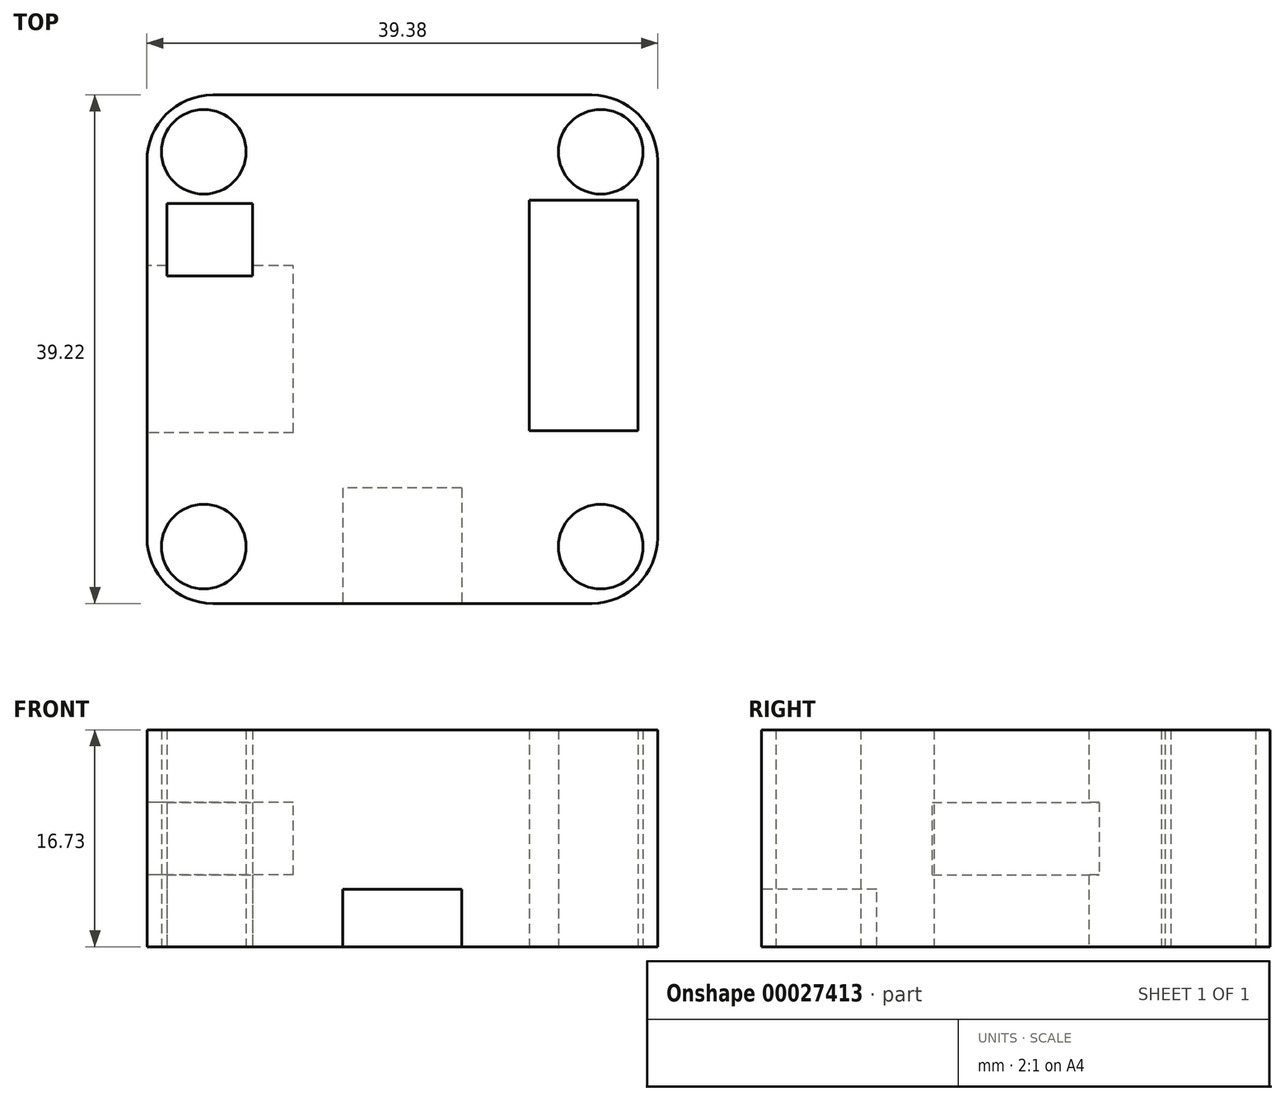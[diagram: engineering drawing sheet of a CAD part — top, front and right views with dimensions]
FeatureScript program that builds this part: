
annotation { "Feature Type Name" : "Feature", "Feature Type Description" : "" }
export const myFeature = defineFeature(function(context is Context, id is Id, definition is map)
    precondition{}
    {
        {
            var Q0;
            Q0=qCreatedBy(makeId("Top.planeOp"),FACE);
            var sketch = newSketch(context, id + "F0", { "sketchPlane" : qUnion([Q0])});
            skLineSegment(sketch, "E0.rect.bottom", {"start": v(19.69, -19.6) * mm, "end": v(-19.69, -19.6) * mm});
            skLineSegment(sketch, "E0.rect.top", {"start": v(19.69, 19.6) * mm, "end": v(-19.69, 19.6) * mm});
            skLineSegment(sketch, "E0.rect.left", {"start": v(19.69, -19.6) * mm, "end": v(19.69, 19.6) * mm});
            skLineSegment(sketch, "E0.rect.right", {"start": v(-19.69, -19.6) * mm, "end": v(-19.69, 19.6) * mm});
            skPoint(sketch, "E0.rect.middle", {"position": v(0, 0) * mm});
            skLineSegment(sketch, "E1.bottom", {"start": v(9.78, 11.5) * mm, "end": v(18.19, 11.5) * mm});
            skLineSegment(sketch, "E1.top", {"start": v(9.78, -6.3) * mm, "end": v(18.19, -6.3) * mm});
            skLineSegment(sketch, "E1.left", {"start": v(9.78, 11.5) * mm, "end": v(9.78, -6.3) * mm});
            skLineSegment(sketch, "E1.right", {"start": v(18.19, 11.5) * mm, "end": v(18.19, -6.3) * mm});
            skLineSegment(sketch, "E2.bottom", {"start": v(-18.16, 11.23) * mm, "end": v(-11.56, 11.23) * mm});
            skLineSegment(sketch, "E2.top", {"start": v(-18.16, 5.64) * mm, "end": v(-11.56, 5.64) * mm});
            skLineSegment(sketch, "E2.left", {"start": v(-18.16, 11.23) * mm, "end": v(-18.16, 5.64) * mm});
            skLineSegment(sketch, "E2.right", {"start": v(-11.56, 11.23) * mm, "end": v(-11.56, 5.64) * mm});
            skCircle(sketch, "E3", {"center": v(-15.3, -15.23) * mm, "radius": 3.26 * mm});
            skLineSegment(sketch, "E4", {"start": v(0, 0) * mm, "end": v(0, -19.6) * mm, "construction": true});
            skCircle(sketch, "E5.MirrorC", {"center": v(15.3, -15.23) * mm, "radius": 3.26 * mm});
            skLineSegment(sketch, "E6", {"start": v(0, 0) * mm, "end": v(-19.69, 0) * mm, "construction": true});
            skCircle(sketch, "E7.MirrorC", {"center": v(-15.3, 15.23) * mm, "radius": 3.26 * mm});
            skLineSegment(sketch, "E8", {"start": v(0, 0) * mm, "end": v(0, 19.6) * mm, "construction": true});
            skCircle(sketch, "E9.MirrorC", {"center": v(15.3, 15.23) * mm, "radius": 3.26 * mm});
            skSolve(sketch);
        }
        {
            var Q0;
            Q0=makeQuery(id+"F0.imprint","IMPRINT",FACE,{"disambiguationData":[TD([[makeQuery(id+"F0.imprint","IMPRINT",EDGE,{"derivedFrom":sQuery(id+"F0.wireOp",EDGE,"E0.rect.bottom")}),-1.0]])]});
            extrude(context, id + "F1", {"entities" : qUnion([Q0]), "depth" : 16.73 * mm});
        }
        {
            var Q0;
            Q0=makeQuery(id+"F1.opExtrude","SWEPT_EDGE",EDGE,{"disambiguationData":[OSD([sQuery(id+"F0.wireOp",EDGE,"E0.rect.top"),sQuery(id+"F0.wireOp",EDGE,"E0.rect.right")])]});
            var Q1;
            Q1=makeQuery(id+"F1.opExtrude","SWEPT_EDGE",EDGE,{"disambiguationData":[OSD([sQuery(id+"F0.wireOp",EDGE,"E0.rect.top"),sQuery(id+"F0.wireOp",EDGE,"E0.rect.left")])]});
            var Q2;
            Q2=makeQuery(id+"F1.opExtrude","SWEPT_EDGE",EDGE,{"disambiguationData":[OSD([sQuery(id+"F0.wireOp",EDGE,"E0.rect.bottom"),sQuery(id+"F0.wireOp",EDGE,"E0.rect.left")])]});
            var Q3;
            Q3=makeQuery(id+"F1.opExtrude","SWEPT_EDGE",EDGE,{"disambiguationData":[OSD([sQuery(id+"F0.wireOp",EDGE,"E0.rect.bottom"),sQuery(id+"F0.wireOp",EDGE,"E0.rect.right")])]});
            fillet(context, id + "F2", {"entities" : qUnion([Q0, Q1, Q2, Q3]), "radius" : 5.08 * mm, "tangentPropagation" : true, "allowEdgeOverflow" : false});
        }
        {
            var Q0;
            Q0=makeQuery(id+"F1.opExtrude","SWEPT_FACE",FACE,{"disambiguationData":[OSD([sQuery(id+"F0.wireOp",EDGE,"E0.rect.bottom")])]});
            var sketch = newSketch(context, id + "F3", { "sketchPlane" : qUnion([Q0])});
            skLineSegment(sketch, "E10.rect.bottom", {"start": v(4.58, 0) * mm, "end": v(-4.59, 0) * mm});
            skLineSegment(sketch, "E10.rect.top", {"start": v(4.58, 4.43) * mm, "end": v(-4.59, 4.43) * mm});
            skLineSegment(sketch, "E10.rect.left", {"start": v(4.58, 0) * mm, "end": v(4.58, 4.43) * mm});
            skLineSegment(sketch, "E10.rect.right", {"start": v(-4.59, 0) * mm, "end": v(-4.59, 4.43) * mm});
            skPoint(sketch, "E10.rect.middle", {"position": v(0, 2.21) * mm});
            skSolve(sketch);
        }
        {
            var Q0;
            Q0=makeQuery(id+"F3.imprint","IMPRINT",FACE,{"disambiguationData":[TD([[makeQuery(id+"F3.imprint","IMPRINT",EDGE,{"derivedFrom":sQuery(id+"F3.wireOp",EDGE,"E10.rect.bottom")}),-1.0]])]});
            extrude(context, id + "F4", {"entities" : qUnion([Q0]), "operationType" : NewBodyOperationType.REMOVE, "oppositeDirection" : true, "depth" : 8.9 * mm});
        }
        {
            var Q0;
            Q0=makeQuery(id+"F1.opExtrude","SWEPT_FACE",FACE,{"disambiguationData":[OSD([sQuery(id+"F0.wireOp",EDGE,"E0.rect.right")])]});
            var sketch = newSketch(context, id + "F5", { "sketchPlane" : qUnion([Q0])});
            skLineSegment(sketch, "E11.rect.bottom", {"start": v(6.44, 5.54) * mm, "end": v(-6.44, 5.54) * mm});
            skLineSegment(sketch, "E11.rect.top", {"start": v(6.44, 11.14) * mm, "end": v(-6.44, 11.14) * mm});
            skLineSegment(sketch, "E11.rect.left", {"start": v(6.44, 5.54) * mm, "end": v(6.44, 11.14) * mm});
            skLineSegment(sketch, "E11.rect.right", {"start": v(-6.44, 5.54) * mm, "end": v(-6.44, 11.14) * mm});
            skPoint(sketch, "E11.rect.middle", {"position": v(0, 8.34) * mm});
            skSolve(sketch);
        }
        {
            var Q0;
            Q0=makeQuery(id+"F5.imprint","IMPRINT",FACE,{"disambiguationData":[TD([[makeQuery(id+"F5.imprint","IMPRINT",EDGE,{"derivedFrom":sQuery(id+"F5.wireOp",EDGE,"E11.rect.bottom")}),-1.0]])]});
            extrude(context, id + "F6", {"entities" : qUnion([Q0]), "operationType" : NewBodyOperationType.REMOVE, "oppositeDirection" : true, "depth" : 11.28 * mm});
        }
    });
